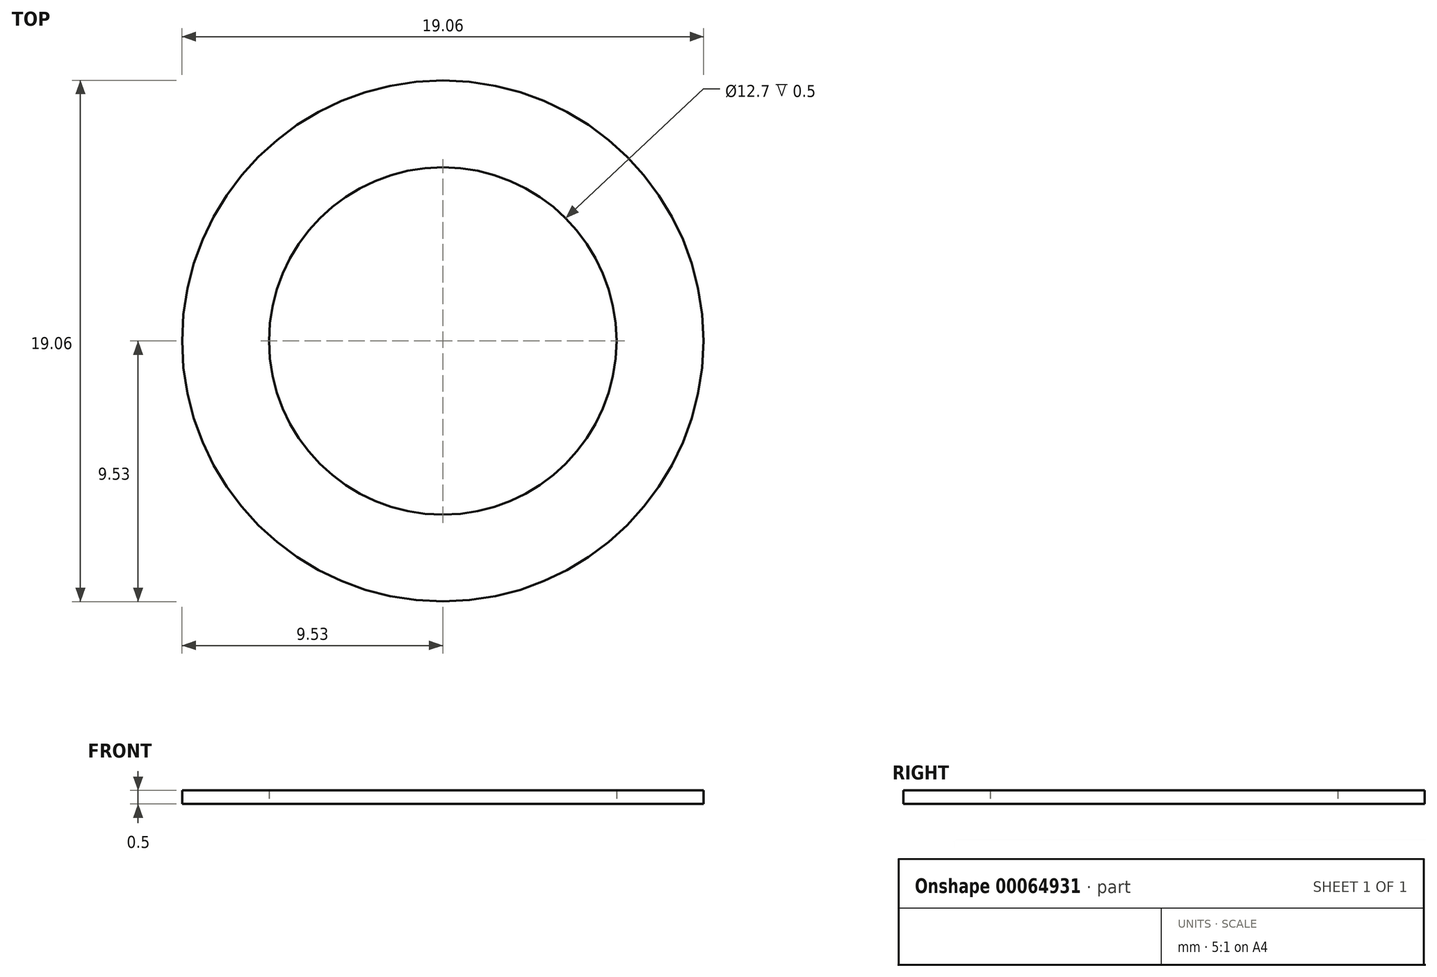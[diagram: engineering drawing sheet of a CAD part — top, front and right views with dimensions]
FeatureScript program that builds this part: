
annotation { "Feature Type Name" : "Feature", "Feature Type Description" : "" }
export const myFeature = defineFeature(function(context is Context, id is Id, definition is map)
    precondition{}
    {
        {
            var Q0;
            Q0=qCreatedBy(makeId("Top.planeOp"),FACE);
            var sketch = newSketch(context, id + "F0", { "sketchPlane" : qUnion([Q0])});
            skCircle(sketch, "E0", {"center": v(0, 0) * mm, "radius": 6.35 * mm});
            skCircle(sketch, "E1", {"center": v(0, 0) * mm, "radius": 9.53 * mm});
            skSolve(sketch);
        }
        {
            var Q0;
            Q0=makeQuery(id+"F0.imprint","IMPRINT",FACE,{"disambiguationData":[TD([[makeQuery(id+"F0.imprint","IMPRINT",EDGE,{"derivedFrom":sQuery(id+"F0.wireOp",EDGE,"E0")}),-1.0]])]});
            extrude(context, id + "F1", {"entities" : qUnion([Q0]), "depth" : .5 * mm});
        }
    });
